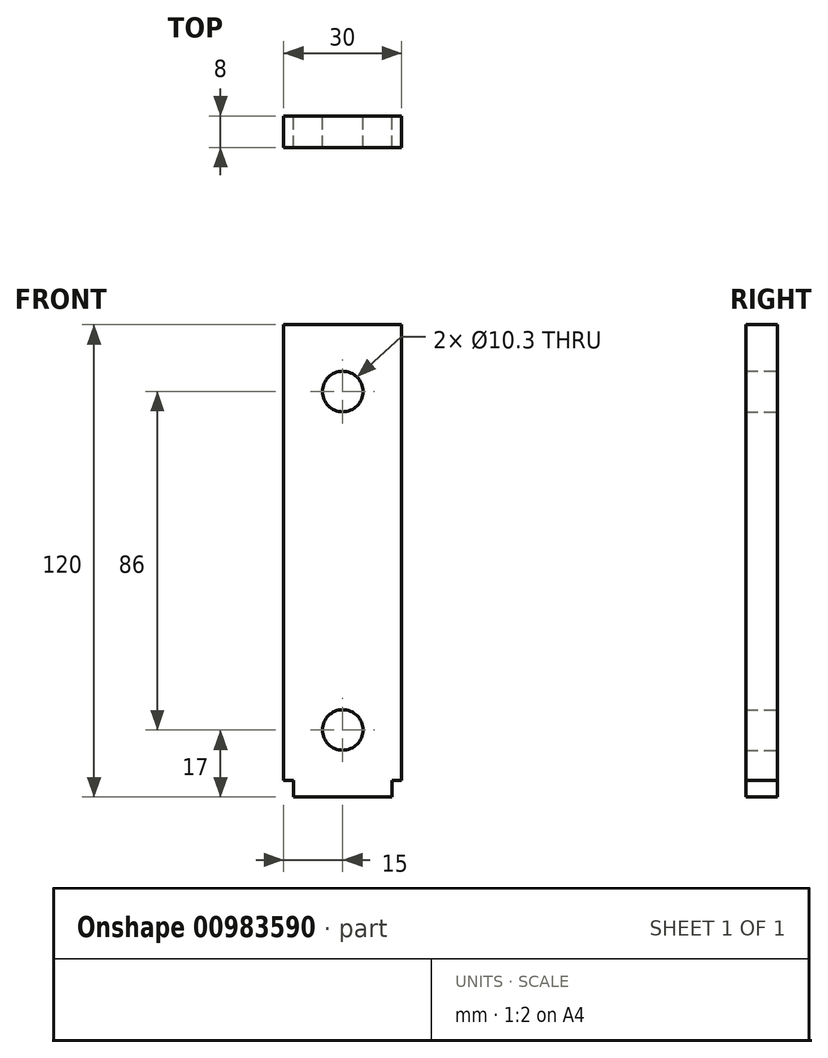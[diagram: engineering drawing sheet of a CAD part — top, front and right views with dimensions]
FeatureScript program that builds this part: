
annotation { "Feature Type Name" : "Feature", "Feature Type Description" : "" }
export const myFeature = defineFeature(function(context is Context, id is Id, definition is map)
    precondition{}
    {
        {
            var Q0;
            Q0=qCreatedBy(makeId("Front.planeOp"),FACE);
            var sketch = newSketch(context, id + "F0", { "sketchPlane" : qUnion([Q0])});
            skLineSegment(sketch, "E0", {"start": v(-15, 0) * mm, "end": v(15, 0) * mm});
            skLineSegment(sketch, "E1", {"start": v(15, 0) * mm, "end": v(15, -115.8) * mm});
            skLineSegment(sketch, "E2", {"start": v(15, -115.8) * mm, "end": v(12.5, -115.8) * mm});
            skLineSegment(sketch, "E3", {"start": v(12.5, -115.8) * mm, "end": v(12.5, -120) * mm});
            skLineSegment(sketch, "E4", {"start": v(12.5, -120) * mm, "end": v(-12.5, -120) * mm});
            skLineSegment(sketch, "E5", {"start": v(-12.5, -120) * mm, "end": v(-12.5, -115.8) * mm});
            skLineSegment(sketch, "E6", {"start": v(-12.5, -115.8) * mm, "end": v(-15, -115.8) * mm});
            skLineSegment(sketch, "E7", {"start": v(-15, -115.8) * mm, "end": v(-15, 0) * mm});
            skCircle(sketch, "E8", {"center": v(0, -17) * mm, "radius": 5.15 * mm});
            skCircle(sketch, "E9", {"center": v(0, -103) * mm, "radius": 5.15 * mm});
            skLineSegment(sketch, "E10", {"start": v(0, 0) * mm, "end": v(0, -120) * mm, "construction": true});
            skCircle(sketch, "E11", {"center": v(0, -17) * mm, "radius": 11 * mm, "construction": true});
            skCircle(sketch, "E12", {"center": v(0, -103) * mm, "radius": 10.76 * mm, "construction": true});
            skLineSegment(sketch, "E13", {"start": v(-15, -4) * mm, "end": v(15, -4) * mm, "construction": true});
            skSolve(sketch);
        }
        {
            var Q0;
            Q0=makeQuery(id+"F0.imprint","IMPRINT",FACE,{"disambiguationData":[TD([[makeQuery(id+"F0.imprint","IMPRINT",EDGE,{"derivedFrom":sQuery(id+"F0.wireOp",EDGE,"E0")}),-1.0]])]});
            extrude(context, id + "F1", {"entities" : qUnion([Q0]), "depth" : 8 * mm, "offsetDistance" : 25.4 * mm, "symmetric" : true});
        }
    });
